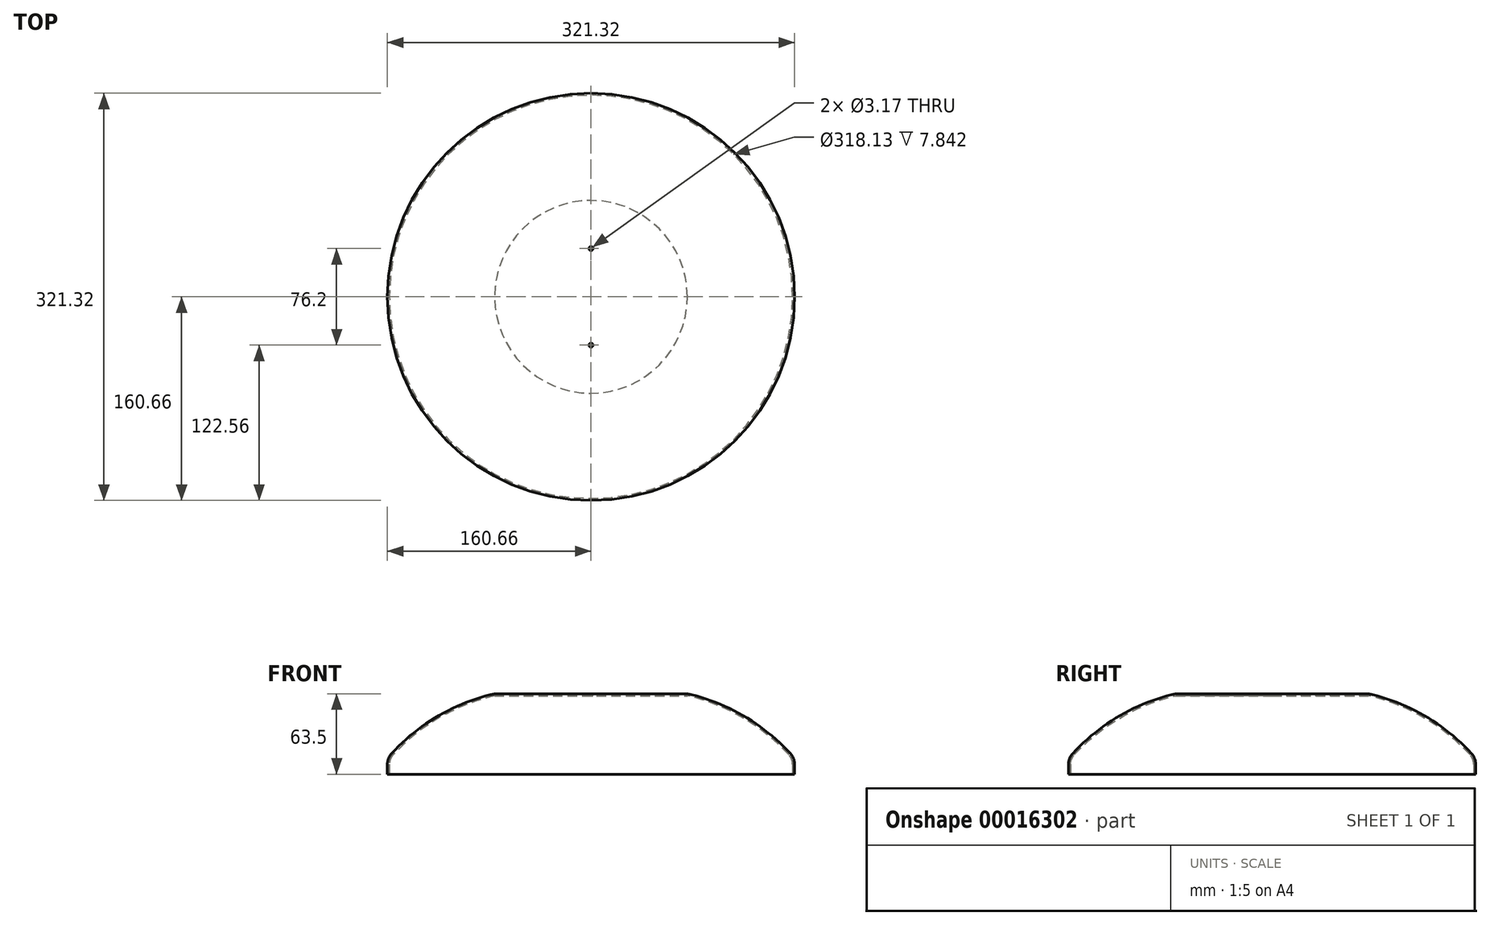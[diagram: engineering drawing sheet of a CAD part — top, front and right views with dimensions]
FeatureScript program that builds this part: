
annotation { "Feature Type Name" : "Feature", "Feature Type Description" : "" }
export const myFeature = defineFeature(function(context is Context, id is Id, definition is map)
    precondition{}
    {
        {
            var Q0;
            Q0=qCreatedBy(makeId("Front.planeOp"),FACE);
            var sketch = newSketch(context, id + "F0", { "sketchPlane" : qUnion([Q0])});
            skLineSegment(sketch, "E0", {"start": v(0, 0) * mm, "end": v(-160.65, 0) * mm});
            skLineSegment(sketch, "E1", {"start": v(0, 0) * mm, "end": v(0, 63.5) * mm});
            skLineSegment(sketch, "E2", {"start": v(0, 63.5) * mm, "end": v(-76.2, 63.5) * mm});
            skLineSegment(sketch, "E3", {"start": v(-160.66, 0) * mm, "end": v(-160.66, 7.84) * mm});
            skArc(sketch, "E4", {"start": v(-76.2, 63.5) * mm, "mid": v(-120.27, 46.08) * mm, "end": v(-157.27, 16.47) * mm});
            skPoint(sketch, "E5.visualSharp", {"position": v(-160.66, 12.7) * mm});
            skArc(sketch, "E5.filletArc", {"start": v(-157.27, 16.47) * mm, "mid": v(-159.78, 12.48) * mm, "end": v(-160.66, 7.84) * mm});
            skSolve(sketch);
        }
        {
            var Q0;
            Q0=makeQuery(id+"F0.imprint","IMPRINT",FACE,{"disambiguationData":[TD([[makeQuery(id+"F0.imprint","IMPRINT",EDGE,{"derivedFrom":sQuery(id+"F0.wireOp",EDGE,"E0")}),-1.0]])]});
            var Q1;
            Q1=sQuery(id+"F0.wireOp",EDGE,"E1");
            revolve(context, id + "F1", {"entities" : qUnion([Q0]), "axis" : qUnion([Q1]), "revolveType" : RevolveType.FULL});
        }
        {
            var Q0;
            Q0=makeQuery(id+"F1.opRevolve","SWEPT_FACE",FACE,{"disambiguationData":[OSD([sQuery(id+"F0.wireOp",EDGE,"E0")])]});
            shell(context, id + "F2", {"entities" : qUnion([Q0]), "thickness" : 1.59 * mm});
        }
        {
            var Q0;
            Q0=makeQuery(id+"F1.opRevolve","SWEPT_EDGE",EDGE,{"disambiguationData":[OSD([sQuery(id+"F0.wireOp",EDGE,"E2"),sQuery(id+"F0.wireOp",EDGE,"E4")])]});
            fillet(context, id + "F3", {"entities" : qUnion([Q0]), "radius" : 25.4 * mm, "tangentPropagation" : true, "allowEdgeOverflow" : false});
        }
        {
            var Q0;
            Q0=makeQuery(id+"F1.opRevolve","SWEPT_FACE",FACE,{"disambiguationData":[OSD([sQuery(id+"F0.wireOp",EDGE,"E2")])]});
            var sketch = newSketch(context, id + "F4", { "sketchPlane" : qUnion([Q0])});
            skCircle(sketch, "E6", {"center": v(0, 38.1) * mm, "radius": 1.59 * mm});
            skCircle(sketch, "E7.MirrorC", {"center": v(0, -38.1) * mm, "radius": 1.59 * mm});
            skSolve(sketch);
        }
        {
            var Q0;
            Q0 = qSketchRegion(id + "F4", true);
            extrude(context, id + "F5", {"entities" : qUnion([Q0]), "operationType" : NewBodyOperationType.REMOVE, "oppositeDirection" : true, "depth" : 25.4 * mm});
        }
    });
